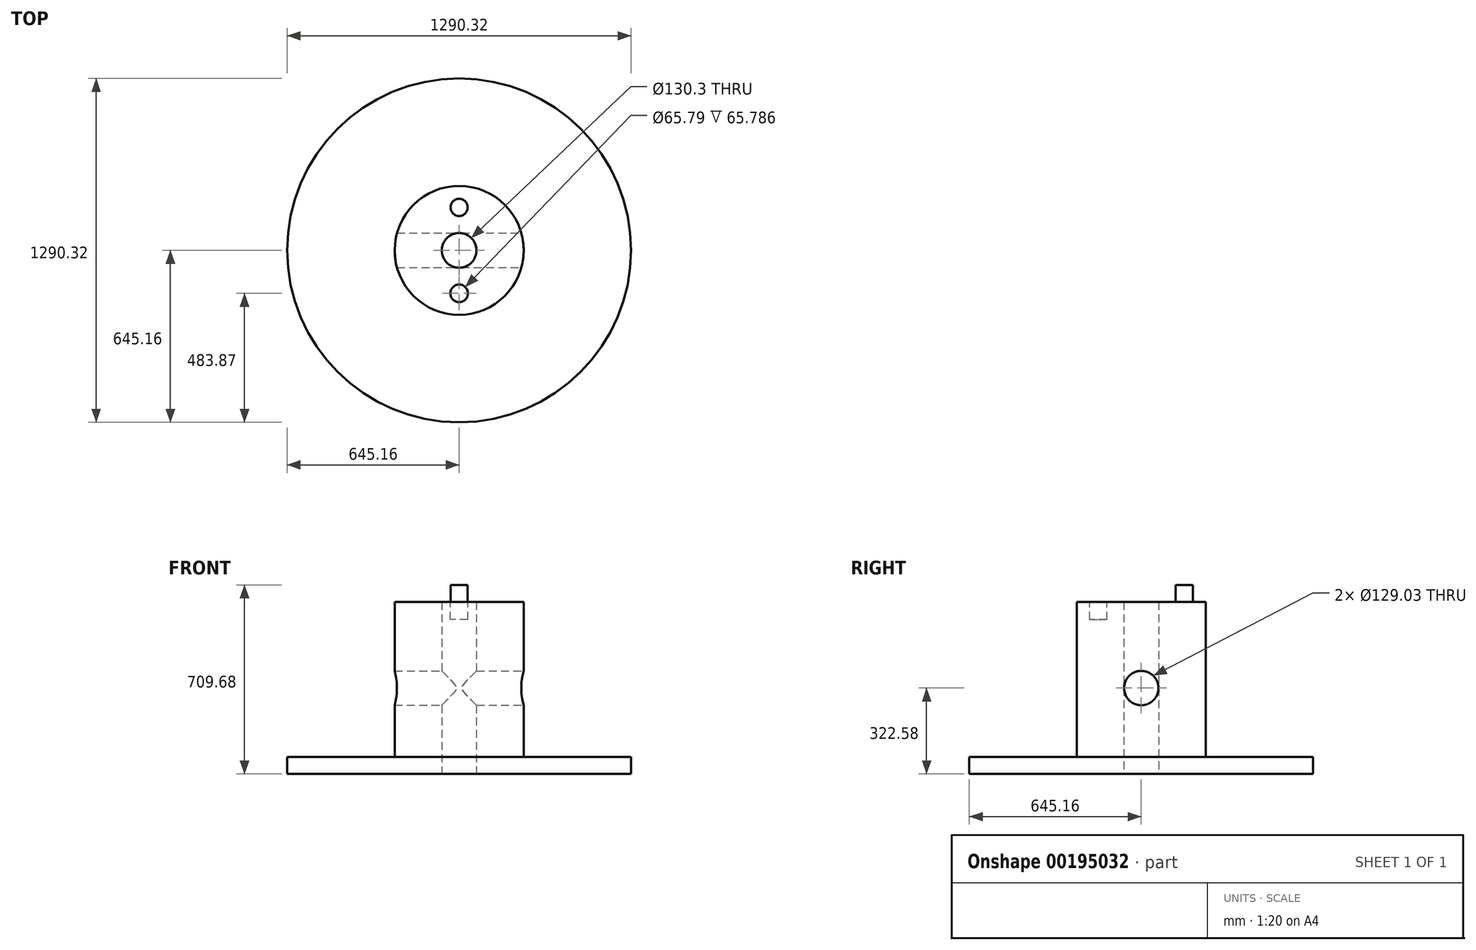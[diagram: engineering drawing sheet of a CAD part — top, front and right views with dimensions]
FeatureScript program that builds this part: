
annotation { "Feature Type Name" : "Feature", "Feature Type Description" : "" }
export const myFeature = defineFeature(function(context is Context, id is Id, definition is map)
    precondition{}
    {
        {
            var Q0;
            Q0=qCreatedBy(makeId("Top.planeOp"),FACE);
            var sketch = newSketch(context, id + "F0", { "sketchPlane" : qUnion([Q0])});
            skCircle(sketch, "E0", {"center": v(0, 0) * mm, "radius": 65.15 * mm});
            skSolve(sketch);
        }
        {
            var Q0;
            Q0=qCreatedBy(makeId("Top.planeOp"),FACE);
            var sketch = newSketch(context, id + "F1", { "sketchPlane" : qUnion([Q0])});
            skCircle(sketch, "E1", {"center": v(0, 0) * mm, "radius": 645.16 * mm});
            skSolve(sketch);
        }
        {
            var Q0;
            Q0=qCreatedBy(makeId("Top.planeOp"),FACE);
            var sketch = newSketch(context, id + "F2", { "sketchPlane" : qUnion([Q0])});
            skCircle(sketch, "E2", {"center": v(0, 0) * mm, "radius": 241.94 * mm});
            skSolve(sketch);
        }
        {
            var Q0;
            Q0=makeQuery(id+"F1.imprint","IMPRINT",FACE,{"disambiguationData":[TD([[makeQuery(id+"F1.imprint","IMPRINT",EDGE,{"derivedFrom":sQuery(id+"F1.wireOp",EDGE,"E1")}),1.0]])]});
            extrude(context, id + "F3", {"entities" : qUnion([Q0]), "depth" : 64.52 * mm});
        }
        {
            var Q0;
            Q0 = qSketchRegion(id + "F2", true);
            extrude(context, id + "F4", {"entities" : qUnion([Q0]), "operationType" : NewBodyOperationType.ADD, "depth" : 645.16 * mm});
        }
        {
            var Q0;
            Q0 = qSketchRegion(id + "F0", true);
            extrude(context, id + "F5", {"entities" : qUnion([Q0]), "operationType" : NewBodyOperationType.REMOVE, "endBound" : BoundingType.THROUGH_ALL, "depth" : 25.4 * mm});
        }
        {
            var Q0;
            Q0=qCreatedBy(makeId("Right.planeOp"),FACE);
            var sketch = newSketch(context, id + "F6", { "sketchPlane" : qUnion([Q0])});
            skCircle(sketch, "E3", {"center": v(0, 322.58) * mm, "radius": 64.52 * mm});
            skSolve(sketch);
        }
        {
            var Q0;
            Q0 = qSketchRegion(id + "F6", true);
            extrude(context, id + "F7", {"entities" : qUnion([Q0]), "operationType" : NewBodyOperationType.REMOVE, "endBound" : BoundingType.SYMMETRIC, "oppositeDirection" : true, "depth" : 254000 * mm});
        }
        {
            var Q0;
            Q0=makeQuery(id+"F4.opExtrude","CAP_FACE",FACE,{"disambiguationData":[OSD([sQuery(id+"F2.wireOp",EDGE,"E2")])],"isStart":false});
            var sketch = newSketch(context, id + "F8", { "sketchPlane" : qUnion([Q0])});
            skCircle(sketch, "E4", {"center": v(0, 161.3) * mm, "radius": 32.26 * mm});
            skSolve(sketch);
        }
        {
            var Q0;
            Q0=makeQuery(id+"F4.opExtrude","CAP_FACE",FACE,{"disambiguationData":[OSD([sQuery(id+"F2.wireOp",EDGE,"E2")])],"isStart":false});
            var sketch = newSketch(context, id + "F9", { "sketchPlane" : qUnion([Q0])});
            skCircle(sketch, "E5", {"center": v(0, -161.29) * mm, "radius": 32.9 * mm});
            skSolve(sketch);
        }
        {
            var Q0;
            Q0 = qSketchRegion(id + "F8", true);
            extrude(context, id + "F10", {"entities" : qUnion([Q0]), "operationType" : NewBodyOperationType.ADD, "depth" : 64.52 * mm});
        }
        {
            var Q0;
            Q0 = qSketchRegion(id + "F9", true);
            extrude(context, id + "F11", {"entities" : qUnion([Q0]), "operationType" : NewBodyOperationType.REMOVE, "oppositeDirection" : true, "depth" : 65.8 * mm});
        }
        {
            var Q0;
            Q0=makeQuery(id+"F3.opExtrude","SWEPT_BODY",BODY,{"disambiguationData":[OSD([sQuery(id+"F1.wireOp",EDGE,"E1")])]});
            transform(context, id + "F12", {"entities" : qUnion([Q0]), "transformType" : TransformType.TRANSLATION_3D, "dx" : 1879.6 * mm, "dy" : 0 * mm, "dz" : 0 * mm, "makeCopy" : true});
        }
        {
            var Q0;
            Q0=makeQuery(id+"F12.opPattern","COPY",BODY,{"derivedFrom":makeQuery(id+"F3.opExtrude","SWEPT_BODY",BODY,{"disambiguationData":[OSD([sQuery(id+"F1.wireOp",EDGE,"E1")])]}),"instanceName":"1"});
            deleteBodies(context, id + "F13", {"entities" : qUnion([Q0])});
        }
    });
